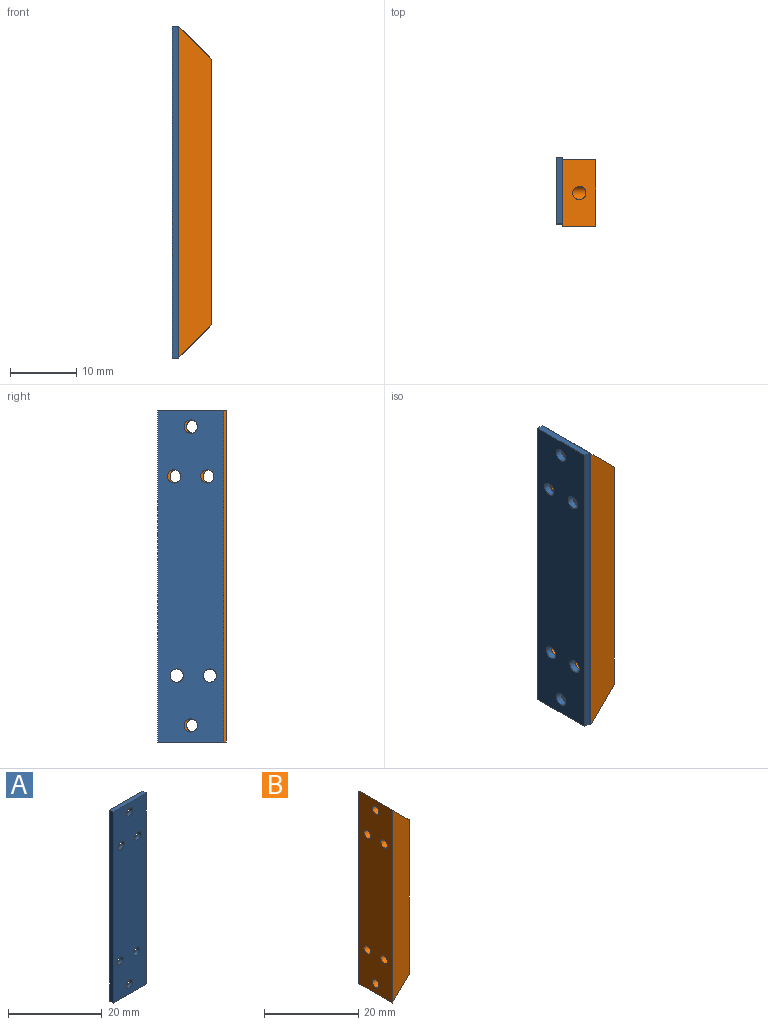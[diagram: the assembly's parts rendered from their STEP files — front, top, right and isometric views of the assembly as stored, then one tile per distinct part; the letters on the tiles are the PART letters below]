
ASSEMBLY  parts=2 mates=1
PART A: 12 faces, bbox 10x1x50 mm
  f0: plane 10x1mm, normal (0,0,-1), area 10mm2, adj f1,f9,f10,f11
  f1: plane 50x1mm, normal (1,0,0), area 50mm2, adj f0,f2,f10,f11
  f2: plane 10x1mm, normal (0,0,1), area 10mm2, adj f1,f9,f10,f11
  f3: cylinder r=1mm len=2mm, axis (0,-1,0), area 6.3mm2, adj f10,f11
  f4: cylinder r=1mm len=2mm, axis (0,-1,0), area 6.3mm2, adj f10,f11
  f5: cylinder r=1mm len=2mm, axis (0,-1,0), area 6.3mm2, adj f10,f11
  f6: cylinder r=1mm len=2mm, axis (0,-1,0), area 6.3mm2, adj f10,f11
  f7: cylinder r=1mm len=2mm, axis (0,-1,0), area 6.3mm2, adj f10,f11
  f8: cylinder r=1mm len=2mm, axis (0,-1,0), area 6.3mm2, adj f10,f11
  f9: plane 50x1mm, normal (-1,0,0), area 50mm2, adj f0,f2,f10,f11
  f10: plane 50x10mm, normal (0,1,0), area 481.2mm2, adj f0,f1,f2,f3,f4,f5,f6,f7
  f11: plane 50x10mm, normal (0,-1,0), area 481.2mm2, adj f0,f1,f2,f3,f4,f5,f6,f7
PART B: 12 faces, bbox 5.4x10.4x50.4 mm
  f0: plane 40x10mm, normal (1,0,0), area 387.4mm2, adj f1,f3,f4,f5,f6,f7,f10,f11
  f1: plane 10x5mm, normal (0.71,0,0.71), area 66.3mm2, adj f0,f2,f4,f5,f9
  f2: plane 50x10mm, normal (-1,0,0), area 481.2mm2, adj f1,f3,f4,f5,f6,f7,f8,f9
  f3: plane 10.42x5.42mm, normal (0.71,0,-0.71), area 66.3mm2, adj f0,f2,f4,f5,f8
  f4: plane 50x5mm, normal (0,1,0), area 225mm2, adj f0,f1,f2,f3
  f5: plane 50x5mm, normal (0,-1,0), area 225mm2, adj f0,f1,f2,f3
  f6: cylinder r=1mm len=5mm, axis (-1,0,0), area 31.4mm2, adj f0,f2
  f7: cylinder r=1mm len=5mm, axis (-1,0,0), area 31.4mm2, adj f0,f2
  f8: cylinder r=1mm len=3.5mm, axis (1,0,0), area 15.7mm2, adj f2,f3
  f9: cylinder r=1mm len=3.5mm, axis (1,0,0), area 15.7mm2, adj f1,f2
  f10: cylinder r=1mm len=5mm, axis (1,0,0), area 31.4mm2, adj f0,f2
  f11: cylinder r=1mm len=5mm, axis (1,0,0), area 31.4mm2, adj f0,f2
PLACE A rot(axis=(0,0,1),90deg) t=(-27.74,9.96,3.73)mm
PLACE B t=(-27.74,-0.42,3.73)mm
MATE fastened A.f6 <-> B.f6  axis (1,0,0) through (-27.74,7.08,13.73)mm
